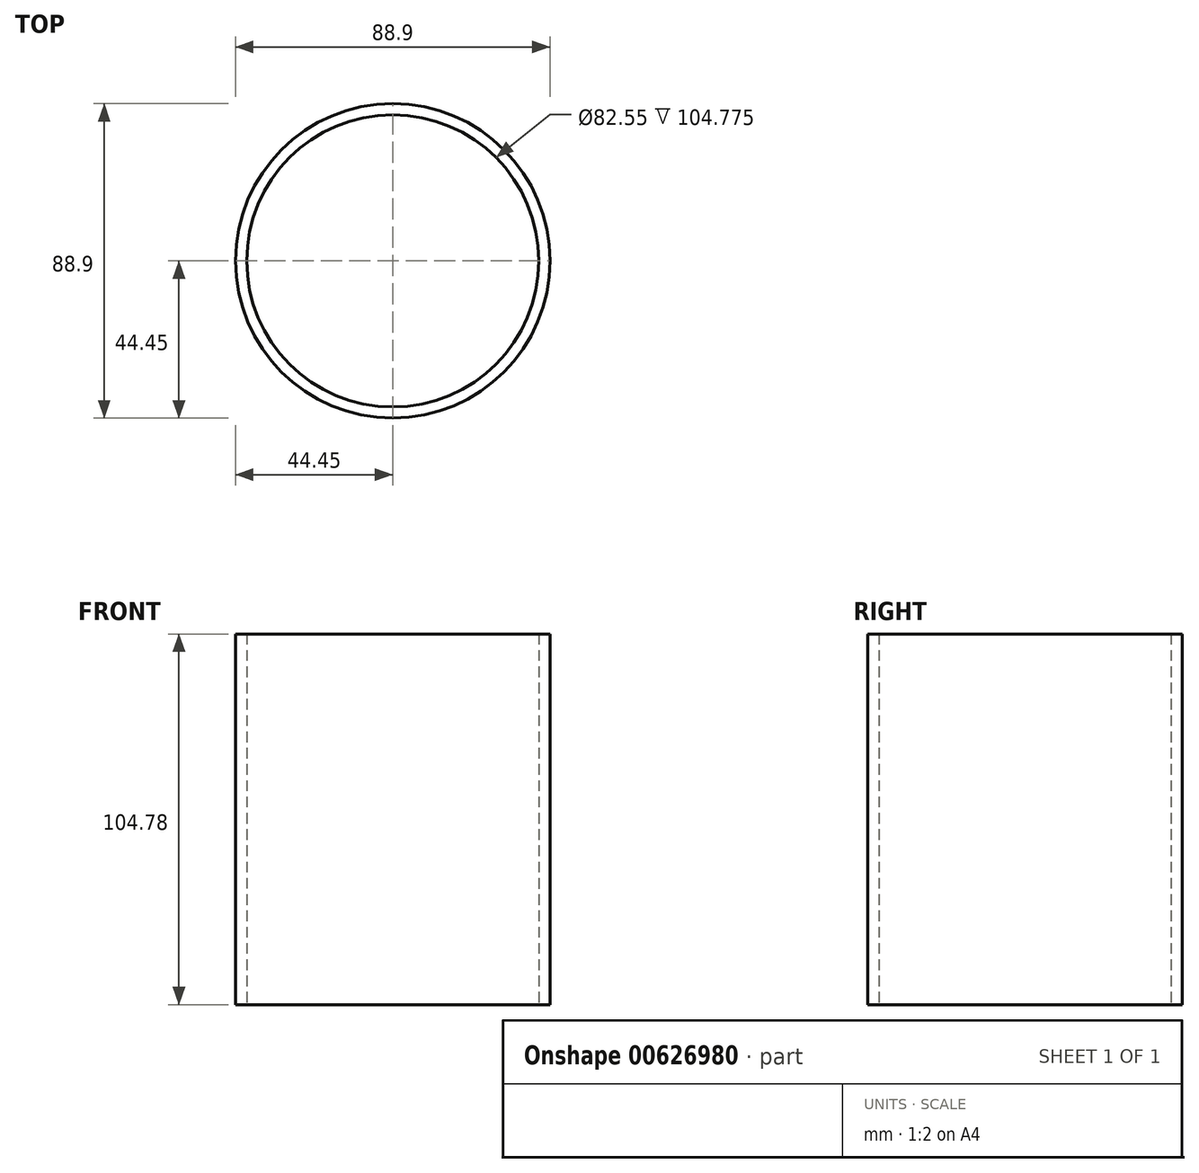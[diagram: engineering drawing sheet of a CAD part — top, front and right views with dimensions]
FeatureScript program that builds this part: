
annotation { "Feature Type Name" : "Feature", "Feature Type Description" : "" }
export const myFeature = defineFeature(function(context is Context, id is Id, definition is map)
    precondition{}
    {
        {
            var Q0;
            Q0=qCreatedBy(makeId("Top.planeOp"),FACE);
            var sketch = newSketch(context, id + "F0", { "sketchPlane" : qUnion([Q0])});
            skCircle(sketch, "E0", {"center": v(0, 0) * mm, "radius": 41.28 * mm});
            skCircle(sketch, "E1", {"center": v(0, 0) * mm, "radius": 44.45 * mm});
            skSolve(sketch);
        }
        {
            var Q0;
            Q0 = qSketchRegion(id + "F0", true);
            extrude(context, id + "F1", {"entities" : qUnion([Q0]), "depth" : 104.77 * mm, "offsetDistance" : 25.4 * mm, "symmetric" : true});
        }
    });
